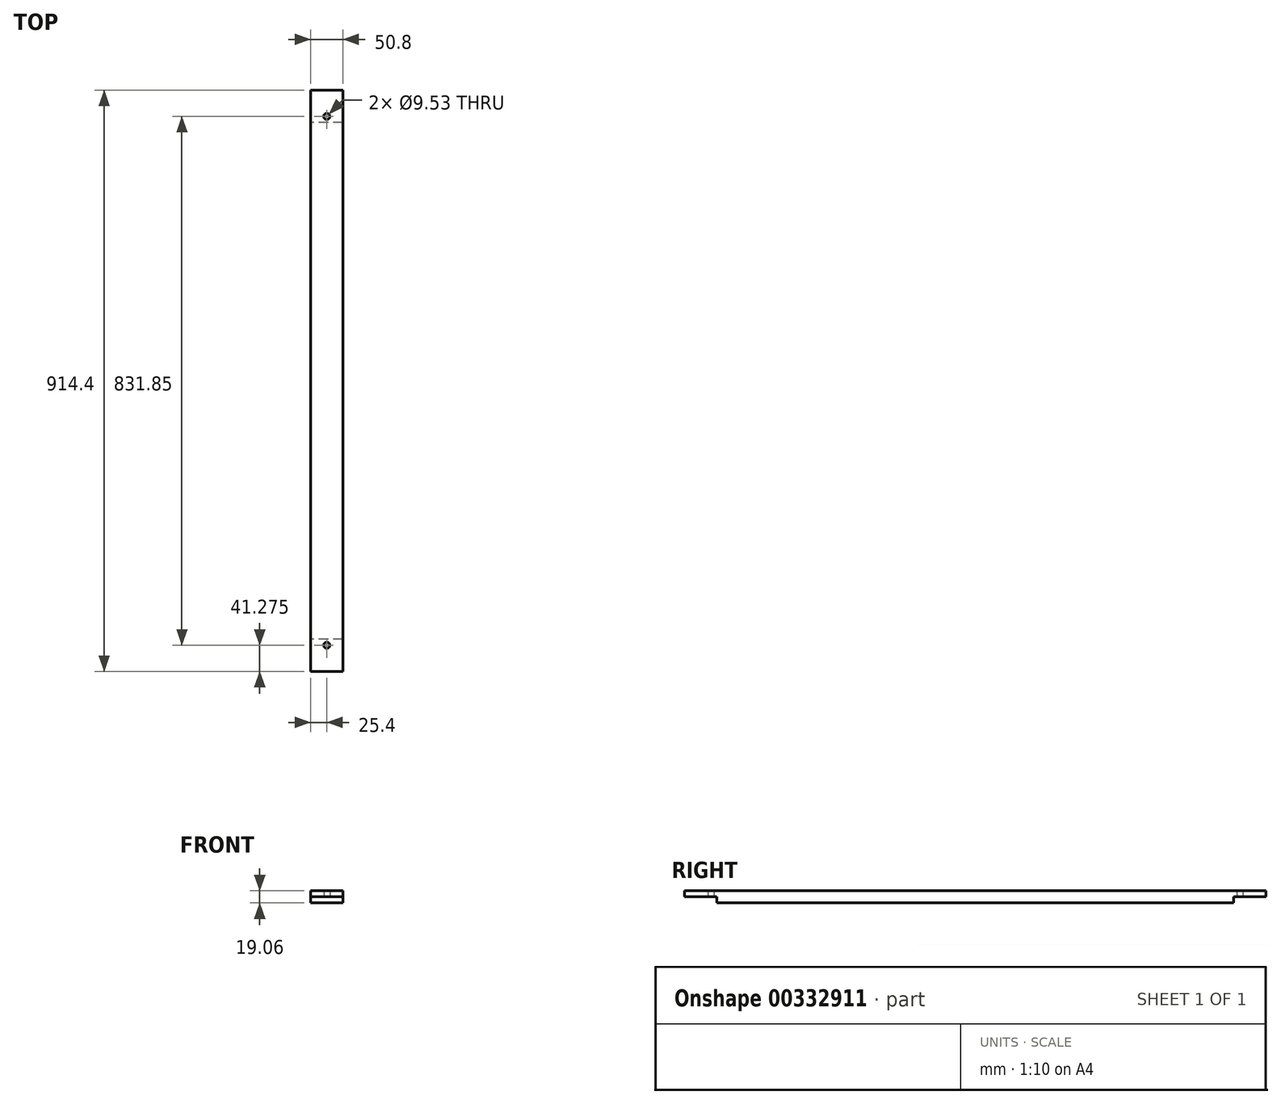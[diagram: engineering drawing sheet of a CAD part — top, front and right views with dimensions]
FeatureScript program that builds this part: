
annotation { "Feature Type Name" : "Feature", "Feature Type Description" : "" }
export const myFeature = defineFeature(function(context is Context, id is Id, definition is map)
    precondition{}
    {
        {
            var Q0;
            Q0=qCreatedBy(makeId("Right.planeOp"),FACE);
            var sketch = newSketch(context, id + "F0", { "sketchPlane" : qUnion([Q0])});
            skLineSegment(sketch, "E0.bottom", {"start": v(-406.4, -9.53) * mm, "end": v(406.4, -9.52) * mm});
            skLineSegment(sketch, "E0.top", {"start": v(-457.2, 9.52) * mm, "end": v(457.2, 9.53) * mm});
            skLineSegment(sketch, "E0.left", {"start": v(-457.2, 0) * mm, "end": v(-457.2, 9.52) * mm});
            skLineSegment(sketch, "E0.right", {"start": v(457.2, 0) * mm, "end": v(457.2, 9.53) * mm});
            skPoint(sketch, "E0.middle", {"position": v(0, 0) * mm});
            skLineSegment(sketch, "E1.bottom", {"start": v(-406.4, 0) * mm, "end": v(-457.2, 0) * mm});
            skLineSegment(sketch, "E1.left", {"start": v(-406.4, 0) * mm, "end": v(-406.4, -9.53) * mm});
            skPoint(sketch, "E1.middle", {"position": v(-465.09, -31.32) * mm});
            skLineSegment(sketch, "E2.bottom", {"start": v(457.2, 0) * mm, "end": v(406.4, 0) * mm});
            skLineSegment(sketch, "E2.right", {"start": v(406.4, 0) * mm, "end": v(406.4, -9.52) * mm});
            skPoint(sketch, "E2.middle", {"position": v(433.95, -23.4) * mm});
            skPoint(sketch, "E3.orphan", {"position": v(406.4, -46.8) * mm});
            skPoint(sketch, "E2.left.end.orphan", {"position": v(461.5, -46.8) * mm});
            skPoint(sketch, "E4.orphan", {"position": v(457.2, -9.52) * mm});
            skPoint(sketch, "E5.orphan", {"position": v(461.5, 0) * mm});
            skPoint(sketch, "E1.top.start.orphan", {"position": v(-406.4, -62.65) * mm});
            skPoint(sketch, "E6.orphan", {"position": v(-457.2, -9.53) * mm});
            skPoint(sketch, "E1.right.end.orphan", {"position": v(-523.77, -62.65) * mm});
            skPoint(sketch, "E1.right.start.orphan", {"position": v(-523.77, 0) * mm});
            skSolve(sketch);
        }
        {
            var Q0;
            Q0 = qSketchRegion(id + "F0", true);
            extrude(context, id + "F1", {"entities" : qUnion([Q0]), "depth" : 50.8 * mm});
        }
        {
            var Q0;
            Q0=makeQuery(id+"F1.opExtrude","SWEPT_FACE",FACE,{"disambiguationData":[OSD([sQuery(id+"F0.wireOp",EDGE,"E0.bottom")])]});
            var sketch = newSketch(context, id + "F2", { "sketchPlane" : qUnion([Q0])});
            skCircle(sketch, "E7", {"center": v(25.4, -415.93) * mm, "radius": 4.76 * mm});
            skCircle(sketch, "E8", {"center": v(25.4, 415.92) * mm, "radius": 4.76 * mm});
            skSolve(sketch);
        }
        {
            var Q0;
            Q0 = qSketchRegion(id + "F2", true);
            extrude(context, id + "F3", {"entities" : qUnion([Q0]), "operationType" : NewBodyOperationType.REMOVE, "oppositeDirection" : true, "depth" : 25.4 * mm});
        }
    });
